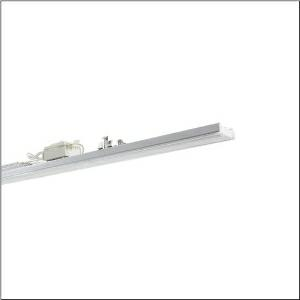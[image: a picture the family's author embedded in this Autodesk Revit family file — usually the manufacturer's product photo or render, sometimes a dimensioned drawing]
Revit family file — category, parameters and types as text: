
# Revit family: licross_11_recessed_mo_51tl18dv6e5g
name_source: partatom
category: Lighting Fixtures
units: mm (PartAtom-declared; Revit-internal decimal feet)

## family parameters
Cut with Voids When Loaded = No
Host = Face
Light Source = No
Part Type = Normal
Room Calculation Point = No
Round Connector Dimension = Use Diameter
Shared = No

## types (1)
- --- (1 x LED, 14560 lm, 84.1 W, 6500K)
    Apparent Load = 84 VA
    CIE Flux Codes = 83 96 99 100 100
    Color Rendering = 80
    Color Temperature = 6500K
    Default Elevation = 1800 mm
    Description = Licross 11 Recessed MO, luminaire insert, of sheet steel, coil coated, white, length: 2.250mm, width: 66mm, height: 67mm, LED rated luminous flux: 14.560lm, light colour: 865, SDCM (Standard Deviation of Colour Matching)MacAdam ≤ 2 SDCM (initial), control gear: DALI 2, with plug, 5-pole, with phase selection, mains connection: 220..240V, AC, 50/60Hz, rated input power: 84W, internal wiring halogen-free, primary light control with lens, of plastic, primary optical cover: cover, of PMMA, light emission: direct distribution, primary light characteristic: symmetric, protection rating (complete): IP40, insulation class (complete): insulation class I (protective earthing), certification: CE, ENEC, VDE, UKCA, protection symbol: D if used in an environment without relevant dust loads with corresponding accessories, impact resistance: IK06, permissible ambient temperature for indoor applications: -25..+35°C, corresponds to IFS (International Featured Standards) requirements for safety and quality in the food industry, reducing of maximum allowable ambient temperature of 5°C with ceiling mounting, LABS conformity tested according to VDMA 24364:2018-05, The light source and the operating device comply with the requirements of the Ecodesign Regulation (EU) 2019/2020 and are replaceable in accordance with this regulation, packaging unit: 1 piece
    Height = 58 mm
    Lamp = 1 x LED
    Lamp Light Flux = 14560 lm
    Lamp Power = 84.1 W
    Lamp count = 1
    Length = 2250 mm
    Luminous efficacy = 173 lm/W
    Manufacturer = Siteco
    ModVariant = No
    Model = 51TL18DV6E5G
    Mounting Place = Ceiling
    Mounting Type = Pendant
    Number of Poles = 1
    OnlyDefault = Yes
    Power Factor = 1
    Product Name = Licross 11 Recessed MO
    Product group = luminaire insert | ceiling pendant
    ProductGroupID = 901
    Protection Class = Protection class I
    Protection Degree = IP 40
    RLX_Detail_Level = 1
    RLX_Emergency_Light_Flux = 0 lm
    RLX_Emergency_Type = 0
    RLX_Emergency_Type_DB = No
    RlxData = <blob elided: 29301 chars, md5=b27eb90c>
    Socket = socket
    Standby Power = 0 W
    System Light Flux = 14560 lm
    System Power = 84 W
    Type Comments = factory setting: luminous flux: 100 % | dim-lin: 254 | 378 mA
    Type Image = l_1296930.jpg
    URL = http://relux.com
    VarID = @adj_037389
    Voltage = 0 V
    Weight = 0.00 kg
    Width = 66 mm

## geometry (parser evidence)
native form markers: Blend x4, Sweep x9
no freeform markers — native parametric forms only
